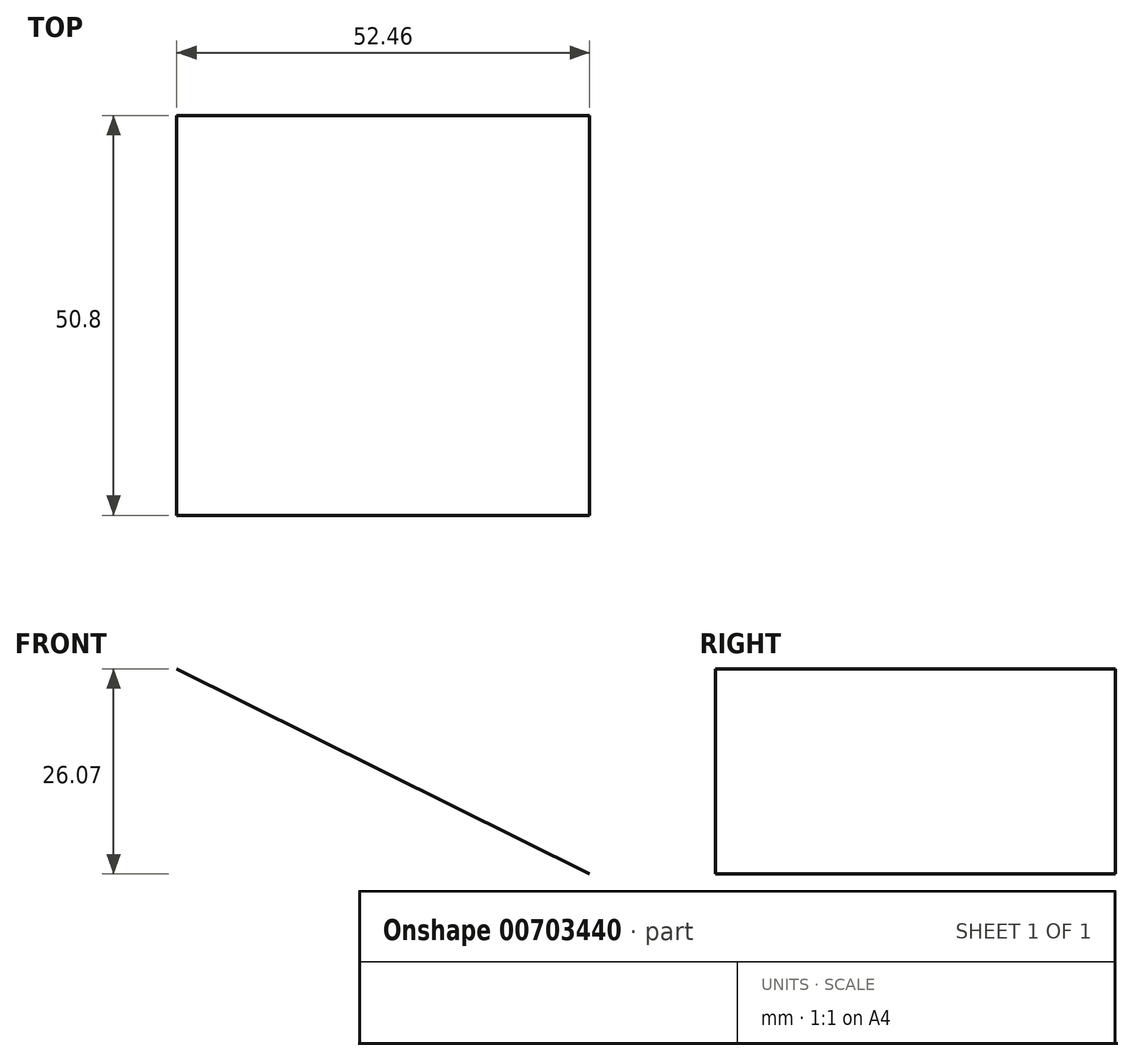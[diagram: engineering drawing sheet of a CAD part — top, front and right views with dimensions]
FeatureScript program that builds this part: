
annotation { "Feature Type Name" : "Feature", "Feature Type Description" : "" }
export const myFeature = defineFeature(function(context is Context, id is Id, definition is map)
    precondition{}
    {
        {
            var Q0;
            Q0=qCreatedBy(makeId("Front.planeOp"),FACE);
            var sketch = newSketch(context, id + "F0", { "sketchPlane" : qUnion([Q0])});
            skCircle(sketch, "E0.cCircle", {"center": v(-91.07, -40.05) * mm, "radius": 109.3 * mm, "construction": true});
            skLineSegment(sketch, "E0.0", {"start": v(-16.2, 44.8) * mm, "end": v(16.2, -4) * mm});
            skLineSegment(sketch, "E0.1", {"start": v(16.2, -4) * mm, "end": v(19.85, -62.47) * mm});
            skLineSegment(sketch, "E0.2", {"start": v(19.85, -62.47) * mm, "end": v(-6.22, -114.92) * mm});
            skLineSegment(sketch, "E0.3", {"start": v(-6.22, -114.92) * mm, "end": v(-55.02, -147.32) * mm});
            skLineSegment(sketch, "E0.4", {"start": v(-55.02, -147.32) * mm, "end": v(-113.49, -150.97) * mm});
            skLineSegment(sketch, "E0.5", {"start": v(-113.49, -150.97) * mm, "end": v(-165.94, -124.9) * mm});
            skLineSegment(sketch, "E0.6", {"start": v(-165.94, -124.9) * mm, "end": v(-198.34, -76.1) * mm});
            skLineSegment(sketch, "E0.7", {"start": v(-198.34, -76.1) * mm, "end": v(-202, -17.63) * mm});
            skLineSegment(sketch, "E0.8", {"start": v(-202, -17.63) * mm, "end": v(-175.92, 34.82) * mm});
            skLineSegment(sketch, "E0.9", {"start": v(-175.92, 34.82) * mm, "end": v(-127.12, 67.22) * mm});
            skLineSegment(sketch, "E0.10", {"start": v(-127.12, 67.22) * mm, "end": v(-68.66, 70.87) * mm});
            skLineSegment(sketch, "E0.11", {"start": v(-68.66, 70.87) * mm, "end": v(-16.2, 44.8) * mm});
            skPoint(sketch, "E0.0.midPoint", {"position": v(0, 20.4) * mm});
            skSolve(sketch);
        }
        {
            var Q0;
            Q0=makeQuery(id+"F0.imprint","IMPRINT",FACE,{"disambiguationData":[TD([[makeQuery(id+"F0.imprint","IMPRINT",EDGE,{"derivedFrom":sQuery(id+"F0.wireOp",EDGE,"E0.0")}),-1.0]])]});
            var Q1;
            Q1=sQuery(id+"F0.wireOp",EDGE,"E0.11");
            extrude(context, id + "F1", {"entities" : qUnion([Q0]), "bodyType" : ToolBodyType.SURFACE, "operationType" : NewBodyOperationType.ADD, "surfaceEntities" : qUnion([Q1]), "depth" : 50.8 * mm, "offsetDistance" : 25.4 * mm});
        }
        {
            var Q0;
            Q0 = qSketchRegion(id + "F0", true);
            extrude(context, id + "F2", {"entities" : qUnion([Q0]), "depth" : 25.4 * mm, "offsetDistance" : 25.4 * mm});
        }
        {
            var Q0;
            Q0=makeQuery(id+"F2.opExtrude","CAP_FACE",FACE,{"disambiguationData":[OSD([sQuery(id+"F0.wireOp",EDGE,"E0.0"),sQuery(id+"F0.wireOp",EDGE,"E0.1"),sQuery(id+"F0.wireOp",EDGE,"E0.2"),sQuery(id+"F0.wireOp",EDGE,"E0.3"),sQuery(id+"F0.wireOp",EDGE,"E0.4"),sQuery(id+"F0.wireOp",EDGE,"E0.5"),sQuery(id+"F0.wireOp",EDGE,"E0.6"),sQuery(id+"F0.wireOp",EDGE,"E0.7"),sQuery(id+"F0.wireOp",EDGE,"E0.8"),sQuery(id+"F0.wireOp",EDGE,"E0.9"),sQuery(id+"F0.wireOp",EDGE,"E0.10"),sQuery(id+"F0.wireOp",EDGE,"E0.11")])],"isStart":false});
            var sketch = newSketch(context, id + "F3", { "sketchPlane" : qUnion([Q0])});
            skSolve(sketch);
        }
        {
            var Q0;
            Q0=makeQuery(id+"F3.imprint","IMPRINT",FACE,{"disambiguationData":[TD([[makeQuery(id+"F3.imprint","IMPRINT",EDGE,{"derivedFrom":makeQuery(id+"F2.opExtrude","CAP_EDGE",EDGE,{"disambiguationData":[OSD([sQuery(id+"F0.wireOp",EDGE,"E0.0")])],"isStart":false})}),-1.0]])]});
            extrude(context, id + "F4", {"entities" : qUnion([Q0]), "operationType" : NewBodyOperationType.REMOVE, "oppositeDirection" : true, "depth" : 6.35 * mm, "offsetDistance" : 25.4 * mm});
        }
        {
            var Q0;
            Q0=makeQuery(id+"F1.opExtrude","SWEPT_FACE",FACE,{"disambiguationData":[OSD([sQuery(id+"F0.wireOp",EDGE,"E0.11")])]});
            var sketch = newSketch(context, id + "F5", { "sketchPlane" : qUnion([Q0])});
            skLineSegment(sketch, "E1.bottom", {"start": v(-159.55, -43.63) * mm, "end": v(40.72, -43.63) * mm});
            skLineSegment(sketch, "E1.top", {"start": v(-159.55, 108.42) * mm, "end": v(40.72, 108.42) * mm});
            skLineSegment(sketch, "E1.left", {"start": v(-159.55, -43.63) * mm, "end": v(-159.55, 108.42) * mm});
            skLineSegment(sketch, "E1.right", {"start": v(40.72, -43.63) * mm, "end": v(40.72, 108.42) * mm});
            skSolve(sketch);
        }
        {
            var Q0;
            Q0=makeQuery(id+"F5.imprint","IMPRINT",FACE,{"disambiguationData":[TD([[makeQuery(id+"F5.imprint","IMPRINT",EDGE,{"derivedFrom":makeQuery(id+"F1.opExtrude","SWEPT_EDGE",EDGE,{"disambiguationData":[OSD([sQuery(id+"F0.wireOp",VERTEX,"E0.11.start")])]})}),-1.0]])]});
            extrude(context, id + "F6", {"entities" : qUnion([Q0]), "operationType" : NewBodyOperationType.ADD, "depth" : 25.4 * mm, "offsetDistance" : 25.4 * mm});
        }
        {
            var Q0;
            Q0=makeQuery(id+"F2.opExtrude","SWEPT_BODY",BODY,{"disambiguationData":[OSD([sQuery(id+"F0.wireOp",EDGE,"E0.0"),sQuery(id+"F0.wireOp",EDGE,"E0.1"),sQuery(id+"F0.wireOp",EDGE,"E0.2"),sQuery(id+"F0.wireOp",EDGE,"E0.3"),sQuery(id+"F0.wireOp",EDGE,"E0.4"),sQuery(id+"F0.wireOp",EDGE,"E0.5"),sQuery(id+"F0.wireOp",EDGE,"E0.6"),sQuery(id+"F0.wireOp",EDGE,"E0.7"),sQuery(id+"F0.wireOp",EDGE,"E0.8"),sQuery(id+"F0.wireOp",EDGE,"E0.9"),sQuery(id+"F0.wireOp",EDGE,"E0.10"),sQuery(id+"F0.wireOp",EDGE,"E0.11")])]});
            var Q1;
            {var subQ0=sQuery(id+"F0.wireOp",EDGE,"E0.11");Q1=makeQuery(id+"F6.opExtrude","SWEPT_FACE",FACE,{"disambiguationData":[OSD([subQ0]),TDD([makeQuery(id+"F5.imprint","IMPRINT",EDGE,{"derivedFrom":makeQuery(id+"F1.opExtrude","CAP_EDGE",EDGE,{"disambiguationData":[OSD([subQ0])],"isStart":false})})])]});}
            mirror(context, id + "F7", {"operationType" : NewBodyOperationType.ADD, "entities" : qUnion([Q0]), "mirrorPlane" : qUnion([Q1])});
        }
        {
            var Q0;
            Q0=makeQuery(id+"F7.opPattern","COPY",FACE,{"derivedFrom":makeQuery(id+"F2.opExtrude","CAP_FACE",FACE,{"disambiguationData":[OSD([sQuery(id+"F0.wireOp",EDGE,"E0.0"),sQuery(id+"F0.wireOp",EDGE,"E0.1"),sQuery(id+"F0.wireOp",EDGE,"E0.2"),sQuery(id+"F0.wireOp",EDGE,"E0.3"),sQuery(id+"F0.wireOp",EDGE,"E0.4"),sQuery(id+"F0.wireOp",EDGE,"E0.5"),sQuery(id+"F0.wireOp",EDGE,"E0.6"),sQuery(id+"F0.wireOp",EDGE,"E0.7"),sQuery(id+"F0.wireOp",EDGE,"E0.8"),sQuery(id+"F0.wireOp",EDGE,"E0.9"),sQuery(id+"F0.wireOp",EDGE,"E0.10"),sQuery(id+"F0.wireOp",EDGE,"E0.11")])],"isStart":true}),"instanceName":"1"});
            var sketch = newSketch(context, id + "F8", { "sketchPlane" : qUnion([Q0])});
            skCircle(sketch, "E2.cCircle", {"center": v(-125.13, -17.63) * mm, "radius": 44.66 * mm, "construction": true});
            skPoint(sketch, "E2.0.midPoint", {"position": v(-169.05, -25.71) * mm});
            skPoint(sketch, "E2.1.start.orphan", {"position": v(-172, -9.72) * mm});
            skPoint(sketch, "E2.0.start.orphan", {"position": v(-166.11, -41.7) * mm});
            skPoint(sketch, "E3.orphan", {"position": v(-78.38, -9.04) * mm});
            skSolve(sketch);
        }
        {
            var Q0;
            Q0 = qSketchRegion(id + "F8", true);
            var Q1;
            Q1=makeQuery(id+"F8.imprint","IMPRINT",FACE,{"disambiguationData":[TD([[makeQuery(id+"F8.imprint","IMPRINT",EDGE,{"derivedFrom":makeQuery(id+"F7.opPattern","COPY",EDGE,{"derivedFrom":makeQuery(id+"F2.opExtrude","CAP_EDGE",EDGE,{"disambiguationData":[OSD([sQuery(id+"F0.wireOp",EDGE,"E0.0")])],"isStart":true}),"instanceName":"1"})}),-1.0]])]});
            extrude(context, id + "F9", {"entities" : qUnion([Q0, Q1]), "operationType" : NewBodyOperationType.REMOVE, "oppositeDirection" : true, "depth" : 127 * mm, "offsetDistance" : 25.4 * mm});
        }
    });
